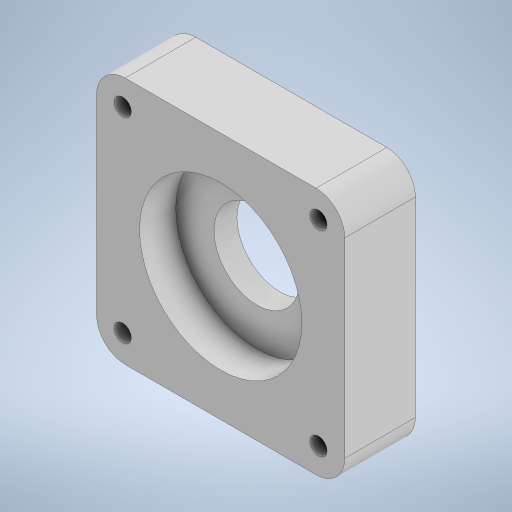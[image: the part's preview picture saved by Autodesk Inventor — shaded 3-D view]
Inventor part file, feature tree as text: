
AUTODESK INVENTOR PART (.ipt)
format: ipt  version: 2024 (Build 280153000, 153)  size: 279,552 bytes
history: native  units: in
note: dims shown in document units (in); Inventor stores cm internally (conversion verified against a paired STEP export)
features: extrude x4, sketch x4, fillet x1
ambient origin geometry x8: Origin, YZ Plane, XZ Plane, XY Plane, X Axis, Y Axis, Z Axis, Center Point
bodies: Body1 (feature_tree)
feature tree (9):
  extrude  "Extrusion6"  Depth=5.1181in
  extrude  "Extrusion7"  Depth=2.5591in
  fillet  "Fillet1"  Radius=2.5591in
  extrude  "Extrusion9"  Depth=1.4567in
  extrude  "Extrusion10"  Depth=0.2362in
  sketch  "Sketch6"  dims[d28=5.1181in d29=5.1181in]
  sketch  "Sketch7"  dims[d30=3.3465in d31=2.5591in d32=2.5591in]
  sketch  "Sketch9"  dims[d33=1.4567in d34=0.0in d36=2.0183in]
  sketch  "Sketch10"  dims[d37=2.0183in d38=0.3543in d39=0.3543in d40=0.3543in d41=0.3543in d42=2.0183in d43=2.0183in d44=2.0183in d45=2.0183in d46=2.0183in d47=2.0183in d48=1.4567in d49=0.0in d50=0.5906in d54=3.3465in d55=1.7717in d56=0.7087in d57=0.0in d58=4.3307in d59=0.2362in d60=0.0in]
